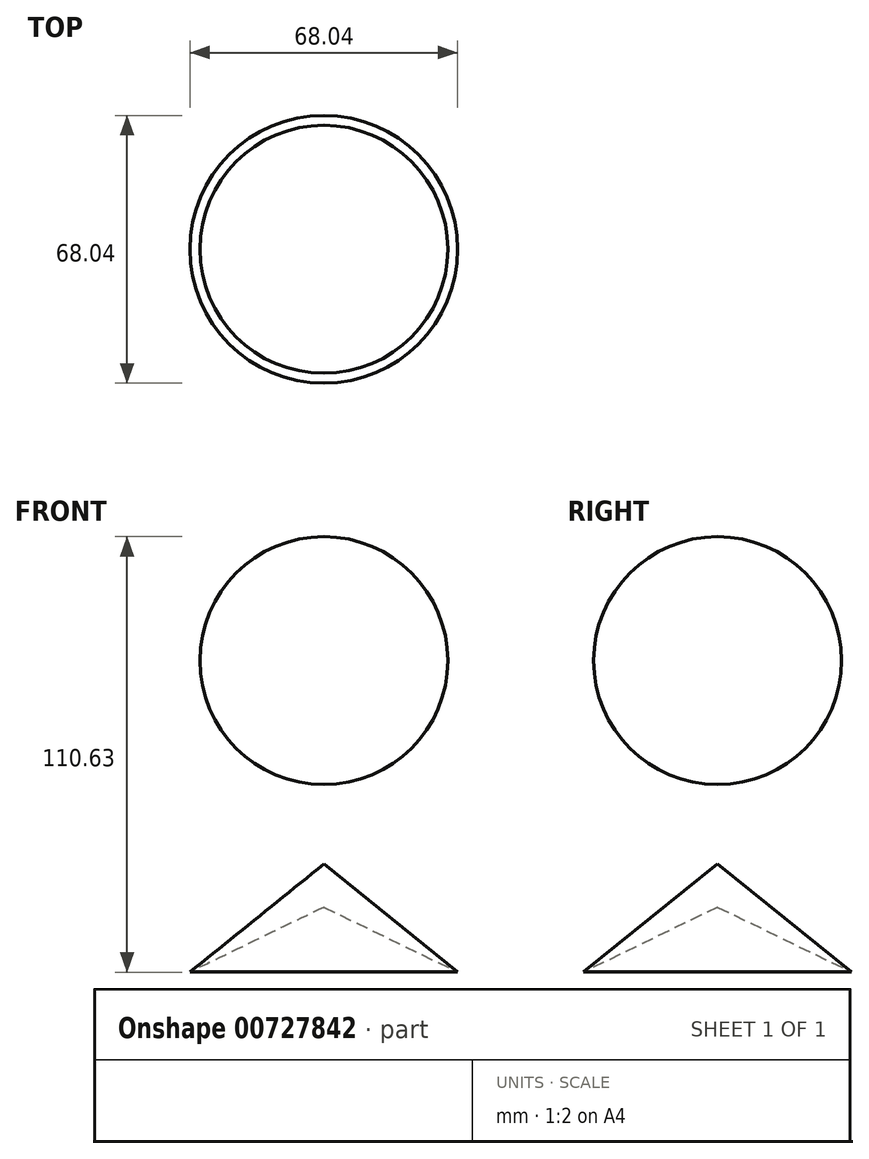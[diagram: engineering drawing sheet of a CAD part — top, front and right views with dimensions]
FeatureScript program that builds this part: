
annotation { "Feature Type Name" : "Feature", "Feature Type Description" : "" }
export const myFeature = defineFeature(function(context is Context, id is Id, definition is map)
    precondition{}
    {
        {
            var Q0;
            Q0=qCreatedBy(makeId("Front.planeOp"),FACE);
            var sketch = newSketch(context, id + "F0", { "sketchPlane" : qUnion([Q0])});
            skCircle(sketch, "E0", {"center": v(0, 62.64) * mm, "radius": 31.5 * mm});
            skLineSegment(sketch, "E1", {"start": v(0, 31.14) * mm, "end": v(0, -34.9) * mm});
            skLineSegment(sketch, "E2", {"start": v(0, -34.9) * mm, "end": v(-24.97, -76.36) * mm});
            skLineSegment(sketch, "E3", {"start": v(-24.97, -76.36) * mm, "end": v(0, -34.9) * mm});
            skLineSegment(sketch, "E4", {"start": v(23.21, -75.78) * mm, "end": v(0, -34.9) * mm});
            skLineSegment(sketch, "E5", {"start": v(0, 10.95) * mm, "end": v(32.27, -8.61) * mm});
            skLineSegment(sketch, "E6", {"start": v(32.27, -8.61) * mm, "end": v(0, 10.95) * mm});
            skLineSegment(sketch, "E7", {"start": v(0, 10.95) * mm, "end": v(-34.02, -16.5) * mm});
            skLineSegment(sketch, "E8", {"start": v(0, 31.14) * mm, "end": v(0, 94.13) * mm});
            skLineSegment(sketch, "E9", {"start": v(0, 94.13) * mm, "end": v(-16.5, 56.1) * mm});
            skLineSegment(sketch, "E10", {"start": v(-34.02, -16.5) * mm, "end": v(0, 0) * mm});
            skLineSegment(sketch, "E11", {"start": v(32.27, -8.61) * mm, "end": v(0, 0) * mm});
            skLineSegment(sketch, "E12", {"start": v(0, 0) * mm, "end": v(0, -34.9) * mm});
            skLineSegment(sketch, "E13", {"start": v(-24.97, -76.36) * mm, "end": v(0, -45.83) * mm});
            skLineSegment(sketch, "E14", {"start": v(23.21, -76.36) * mm, "end": v(0, -45.83) * mm});
            skSolve(sketch);
        }
        {
            var Q0;
            {var subQ0=sQuery(id+"F0.wireOp",EDGE,"E8");Q0=makeQuery(id+"F0.imprint","IMPRINT",FACE,{"disambiguationData":[TD([[makeQuery(id+"F0.imprint","IMPRINT",EDGE,{"derivedFrom":subQ0}),1.0]])]});}
            var Q1;
            {var subQ2=sQuery(id+"F0.wireOp",EDGE,"E7");Q1=makeQuery(id+"F0.imprint","IMPRINT",FACE,{"disambiguationData":[TD([[makeQuery(id+"F0.imprint","IMPRINT",EDGE,{"derivedFrom":subQ2}),1.0]])]});}
            var Q2;
            Q2=sQuery(id+"F0.wireOp",EDGE,"E8");
            revolve(context, id + "F1", {"surfaceOperationType" : NewSurfaceOperationType.NEW, "entities" : qUnion([Q0, Q1]), "axis" : qUnion([Q2]), "revolveType" : RevolveType.FULL});
        }
    });
